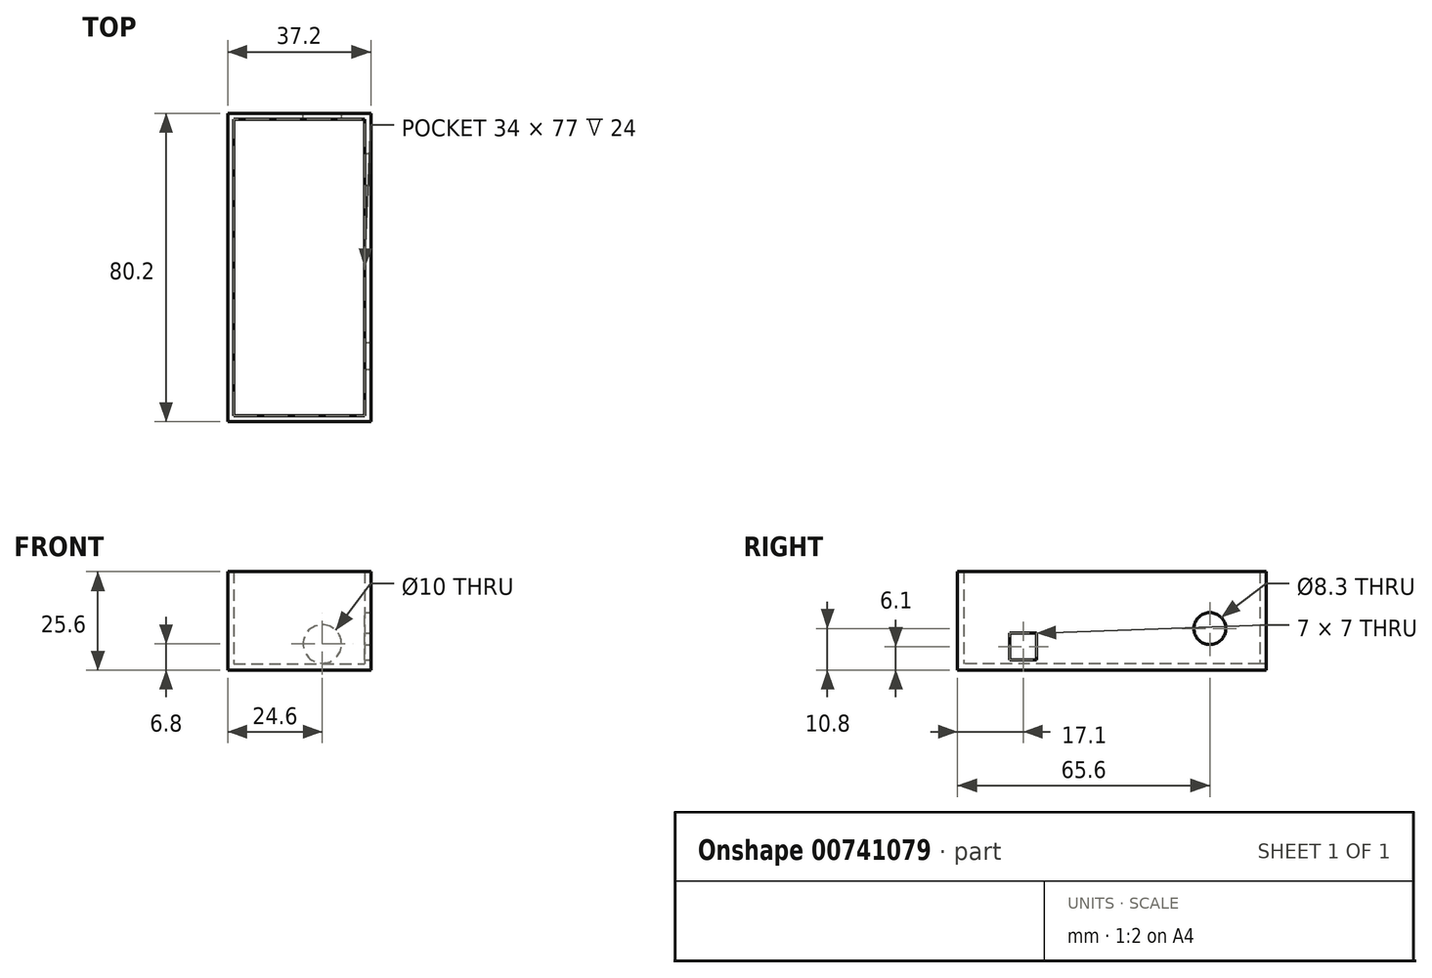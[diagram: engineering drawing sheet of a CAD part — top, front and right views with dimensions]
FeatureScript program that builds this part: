
annotation { "Feature Type Name" : "Feature", "Feature Type Description" : "" }
export const myFeature = defineFeature(function(context is Context, id is Id, definition is map)
    precondition{}
    {
        {
            var Q0;
            Q0=qCreatedBy(makeId("Top.planeOp"),FACE);
            var sketch = newSketch(context, id + "F0", { "sketchPlane" : qUnion([Q0])});
            skLineSegment(sketch, "E0.bottom", {"start": v(-17, 38.5) * mm, "end": v(17, 38.5) * mm});
            skLineSegment(sketch, "E0.top", {"start": v(-17, -38.5) * mm, "end": v(17, -38.5) * mm});
            skLineSegment(sketch, "E0.left", {"start": v(-17, 38.5) * mm, "end": v(-17, -38.5) * mm});
            skLineSegment(sketch, "E0.right", {"start": v(17, 38.5) * mm, "end": v(17, -38.5) * mm});
            skPoint(sketch, "E0.middle", {"position": v(0, 0) * mm});
            skLineSegment(sketch, "E1.bottom", {"start": v(-18.6, 40.1) * mm, "end": v(18.6, 40.1) * mm});
            skLineSegment(sketch, "E1.top", {"start": v(-18.6, -40.1) * mm, "end": v(18.6, -40.1) * mm});
            skLineSegment(sketch, "E1.left", {"start": v(-18.6, 40.1) * mm, "end": v(-18.6, -40.1) * mm});
            skLineSegment(sketch, "E1.right", {"start": v(18.6, 40.1) * mm, "end": v(18.6, -40.1) * mm});
            skSolve(sketch);
        }
        {
            var Q0;
            Q0=makeQuery(id+"F0.imprint","IMPRINT",FACE,{"disambiguationData":[TD([[makeQuery(id+"F0.imprint","IMPRINT",EDGE,{"derivedFrom":sQuery(id+"F0.wireOp",EDGE,"E0.bottom")}),-1.0]])]});
            extrude(context, id + "F1", {"entities" : qUnion([Q0]), "depth" : 1.6 * mm, "offsetDistance" : 25 * mm});
        }
        {
            var Q0;
            Q0=makeQuery(id+"F0.imprint","IMPRINT",FACE,{"disambiguationData":[TD([[makeQuery(id+"F0.imprint","IMPRINT",EDGE,{"derivedFrom":sQuery(id+"F0.wireOp",EDGE,"E0.bottom")}),1.0]])]});
            extrude(context, id + "F2", {"entities" : qUnion([Q0]), "operationType" : NewBodyOperationType.ADD, "depth" : 25.6 * mm, "offsetDistance" : 25 * mm});
        }
        {
            var Q0;
            Q0=makeQuery(id+"F2.opExtrude","SWEPT_FACE",FACE,{"disambiguationData":[OSD([sQuery(id+"F0.wireOp",EDGE,"E1.bottom")])]});
            var sketch = newSketch(context, id + "F3", { "sketchPlane" : qUnion([Q0])});
            skCircle(sketch, "E2", {"center": v(-6, 6.8) * mm, "radius": 5 * mm});
            skSolve(sketch);
        }
        {
            var Q0;
            Q0=makeQuery(id+"F3.imprint","IMPRINT",FACE,{"disambiguationData":[TD([[makeQuery(id+"F3.imprint","IMPRINT",EDGE,{"derivedFrom":sQuery(id+"F3.wireOp",EDGE,"E2")}),1.0]])]});
            extrude(context, id + "F4", {"entities" : qUnion([Q0]), "operationType" : NewBodyOperationType.REMOVE, "endBound" : BoundingType.UP_TO_NEXT, "oppositeDirection" : true, "depth" : 25 * mm, "offsetDistance" : 25 * mm});
        }
        {
            var Q0;
            Q0=makeQuery(id+"F2.opExtrude","SWEPT_FACE",FACE,{"disambiguationData":[OSD([sQuery(id+"F0.wireOp",EDGE,"E1.right")])]});
            var sketch = newSketch(context, id + "F5", { "sketchPlane" : qUnion([Q0])});
            skCircle(sketch, "E3", {"center": v(25.5, 10.8) * mm, "radius": 4.15 * mm});
            skLineSegment(sketch, "E4.bottom", {"start": v(-26.5, 9.6) * mm, "end": v(-19.5, 9.6) * mm});
            skLineSegment(sketch, "E4.top", {"start": v(-26.5, 2.6) * mm, "end": v(-19.5, 2.6) * mm});
            skLineSegment(sketch, "E4.left", {"start": v(-26.5, 9.6) * mm, "end": v(-26.5, 2.6) * mm});
            skLineSegment(sketch, "E4.right", {"start": v(-19.5, 9.6) * mm, "end": v(-19.5, 2.6) * mm});
            skPoint(sketch, "E4.middle", {"position": v(-23, 6.1) * mm});
            skSolve(sketch);
        }
        {
            var Q0;
            Q0=makeQuery(id+"F5.imprint","IMPRINT",FACE,{"disambiguationData":[TD([[makeQuery(id+"F5.imprint","IMPRINT",EDGE,{"derivedFrom":sQuery(id+"F5.wireOp",EDGE,"E3")}),1.0]])]});
            var Q1;
            Q1=makeQuery(id+"F5.imprint","IMPRINT",FACE,{"disambiguationData":[TD([[makeQuery(id+"F5.imprint","IMPRINT",EDGE,{"derivedFrom":sQuery(id+"F5.wireOp",EDGE,"E4.bottom")}),-1.0]])]});
            extrude(context, id + "F6", {"entities" : qUnion([Q0, Q1]), "operationType" : NewBodyOperationType.REMOVE, "endBound" : BoundingType.UP_TO_NEXT, "oppositeDirection" : true, "depth" : 25 * mm, "offsetDistance" : 25 * mm});
        }
    });
